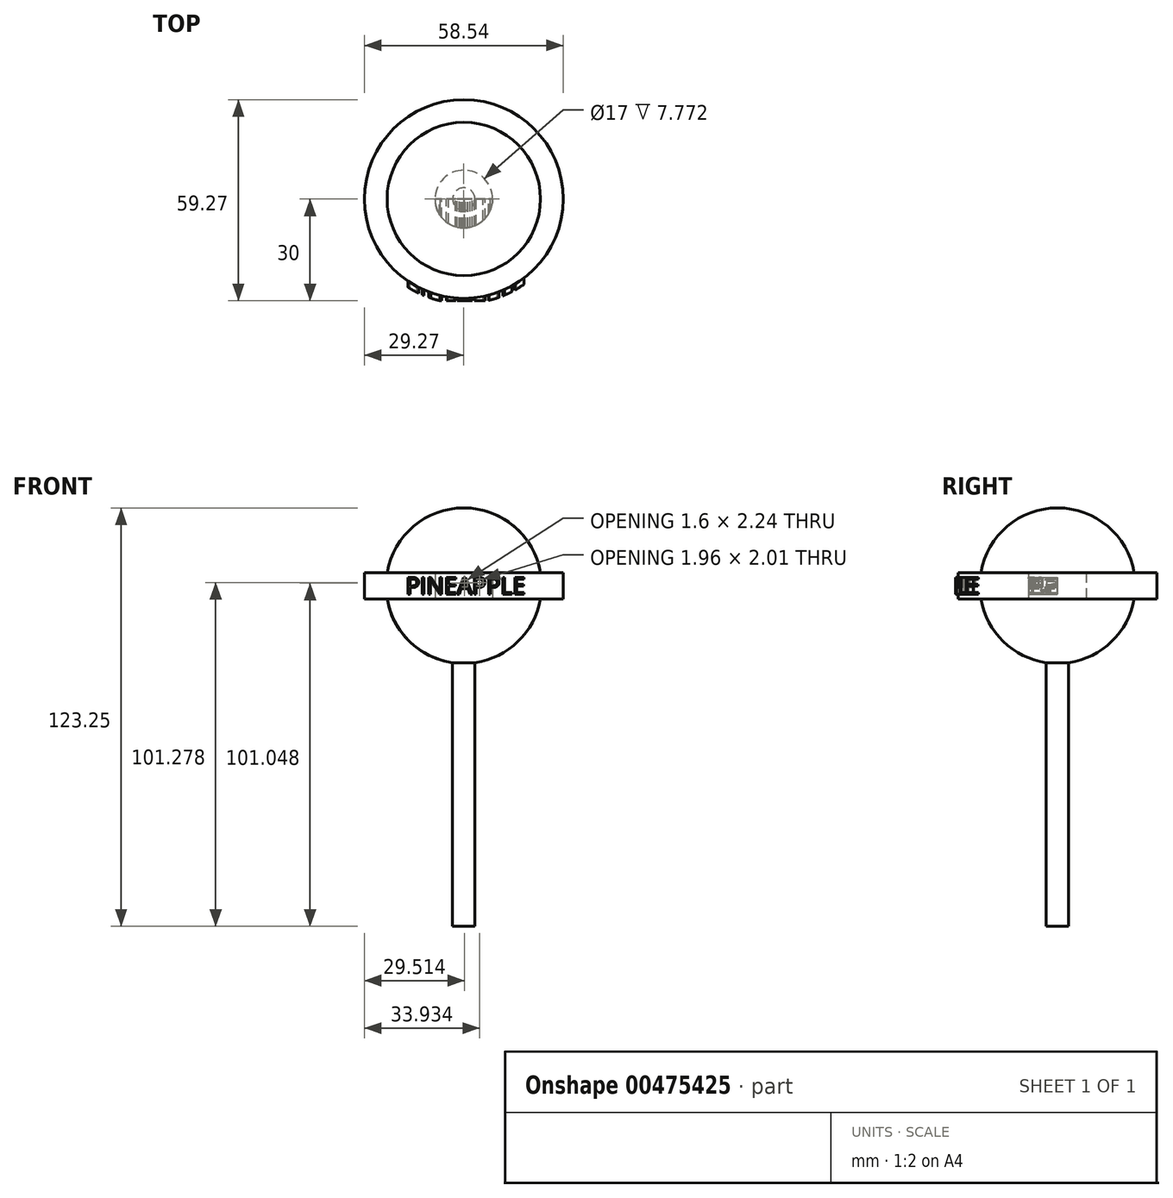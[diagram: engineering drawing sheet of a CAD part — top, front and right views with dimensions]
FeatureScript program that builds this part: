
annotation { "Feature Type Name" : "Feature", "Feature Type Description" : "" }
export const myFeature = defineFeature(function(context is Context, id is Id, definition is map)
    precondition{}
    {
        {
            var Q0;
            Q0=qCreatedBy(makeId("Front.planeOp"),FACE);
            var sketch = newSketch(context, id + "F0", { "sketchPlane" : qUnion([Q0])});
            skArc(sketch, "E0", {"start": v(0, -22.92) * mm, "mid": v(22.92, 0) * mm, "end": v(0, 22.92) * mm});
            skLineSegment(sketch, "E1", {"start": v(0, 22.92) * mm, "end": v(0, -22.92) * mm});
            skLineSegment(sketch, "E2", {"start": v(0, 0) * mm, "end": v(0, 55) * mm, "construction": true});
            skLineSegment(sketch, "E3.bottom", {"start": v(0, 3.89) * mm, "end": v(-0.87, 3.89) * mm});
            skLineSegment(sketch, "E3.top", {"start": v(0, -3.89) * mm, "end": v(-0.87, -3.89) * mm});
            skLineSegment(sketch, "E3.right", {"start": v(-0.87, 3.89) * mm, "end": v(-0.87, -3.89) * mm});
            skLineSegment(sketch, "E4.bottom", {"start": v(29.27, 3.89) * mm, "end": v(-8.5, 3.89) * mm});
            skLineSegment(sketch, "E4.top", {"start": v(29.27, -3.89) * mm, "end": v(-8.5, -3.89) * mm});
            skLineSegment(sketch, "E4.left", {"start": v(29.27, 3.89) * mm, "end": v(29.27, -3.89) * mm});
            skLineSegment(sketch, "E4.right", {"start": v(-8.5, 3.89) * mm, "end": v(-8.5, -3.89) * mm});
            skPoint(sketch, "E4.middle", {"position": v(10.39, 0) * mm});
            skLineSegment(sketch, "E5.bottom", {"start": v(0, -18.65) * mm, "end": v(3.3, -18.65) * mm});
            skLineSegment(sketch, "E5.top", {"start": v(0, -100.33) * mm, "end": v(3.3, -100.33) * mm});
            skLineSegment(sketch, "E5.left", {"start": v(0, -18.65) * mm, "end": v(0, -100.33) * mm});
            skLineSegment(sketch, "E5.right", {"start": v(3.3, -18.65) * mm, "end": v(3.3, -100.33) * mm});
            skSolve(sketch);
        }
        {
            var Q0;
            Q0 = qSketchRegion(id + "F0", true);
            var Q1;
            Q1=sQuery(id+"F0.wireOp",EDGE,"E2");
            revolve(context, id + "F1", {"entities" : qUnion([Q0]), "axis" : qUnion([Q1]), "revolveType" : RevolveType.FULL});
        }
        {
            var Q0;
            Q0=qCreatedBy(makeId("Front.planeOp"),FACE);
            var sketch = newSketch(context, id + "F2", { "sketchPlane" : qUnion([Q0])});
            skText(sketch, "E6", { "text": "PINEAPPLE", "fontName": "OpenSans-Regular.ttf"});
            const initialGuessF2  = {"E6": [-0.0171, -0.00249, 1, 0, 0.00498]};
            skSetInitialGuess(sketch, initialGuessF2);
            skSolve(sketch);
        }
        {
            var Q0;
            Q0 = qSketchRegion(id + "F2", true);
            extrude(context, id + "F3", {"entities" : qUnion([Q0]), "operationType" : NewBodyOperationType.ADD, "depth" : 30 * mm});
        }
        {
            var Q0;
            Q0=qCreatedBy(makeId("Front.planeOp"),FACE);
            var sketch = newSketch(context, id + "F4", { "sketchPlane" : qUnion([Q0])});
            skLineSegment(sketch, "E7", {"start": v(29.27, 3.89) * mm, "end": v(29.27, -3.89) * mm});
            skLineSegment(sketch, "E8.0", {"start": v(30.77, -5.39) * mm, "end": v(23.5, -5.39) * mm});
            skLineSegment(sketch, "E8.1", {"start": v(30.77, 5.39) * mm, "end": v(30.77, -5.39) * mm});
            skLineSegment(sketch, "E8.2", {"start": v(30.77, 5.39) * mm, "end": v(23.4, 5.39) * mm});
            skLineSegment(sketch, "E9", {"start": v(23.4, 5.39) * mm, "end": v(18.61, 19.76) * mm});
            skLineSegment(sketch, "E10", {"start": v(18.61, 19.76) * mm, "end": v(48.43, 19.76) * mm});
            skLineSegment(sketch, "E11", {"start": v(48.43, 19.76) * mm, "end": v(53.55, 5.66) * mm});
            skLineSegment(sketch, "E12", {"start": v(53.55, 5.66) * mm, "end": v(47.67, -19.91) * mm});
            skLineSegment(sketch, "E13", {"start": v(47.67, -19.91) * mm, "end": v(27.86, -23.07) * mm});
            skLineSegment(sketch, "E14", {"start": v(27.86, -23.07) * mm, "end": v(23.5, -5.39) * mm});
            skPoint(sketch, "E15.end.orphan", {"position": v(31.35, 0) * mm});
            skLineSegment(sketch, "E16", {"start": v(0, 0) * mm, "end": v(0, 64.3) * mm, "construction": true});
            skSolve(sketch);
        }
        {
            var Q0;
            Q0 = qSketchRegion(id + "F4", true);
            var Q1;
            Q1=sQuery(id+"F4.wireOp",EDGE,"E16");
            revolve(context, id + "F5", {"operationType" : NewBodyOperationType.REMOVE, "entities" : qUnion([Q0]), "axis" : qUnion([Q1]), "revolveType" : RevolveType.FULL, "oppositeDirection" : true});
        }
    });
